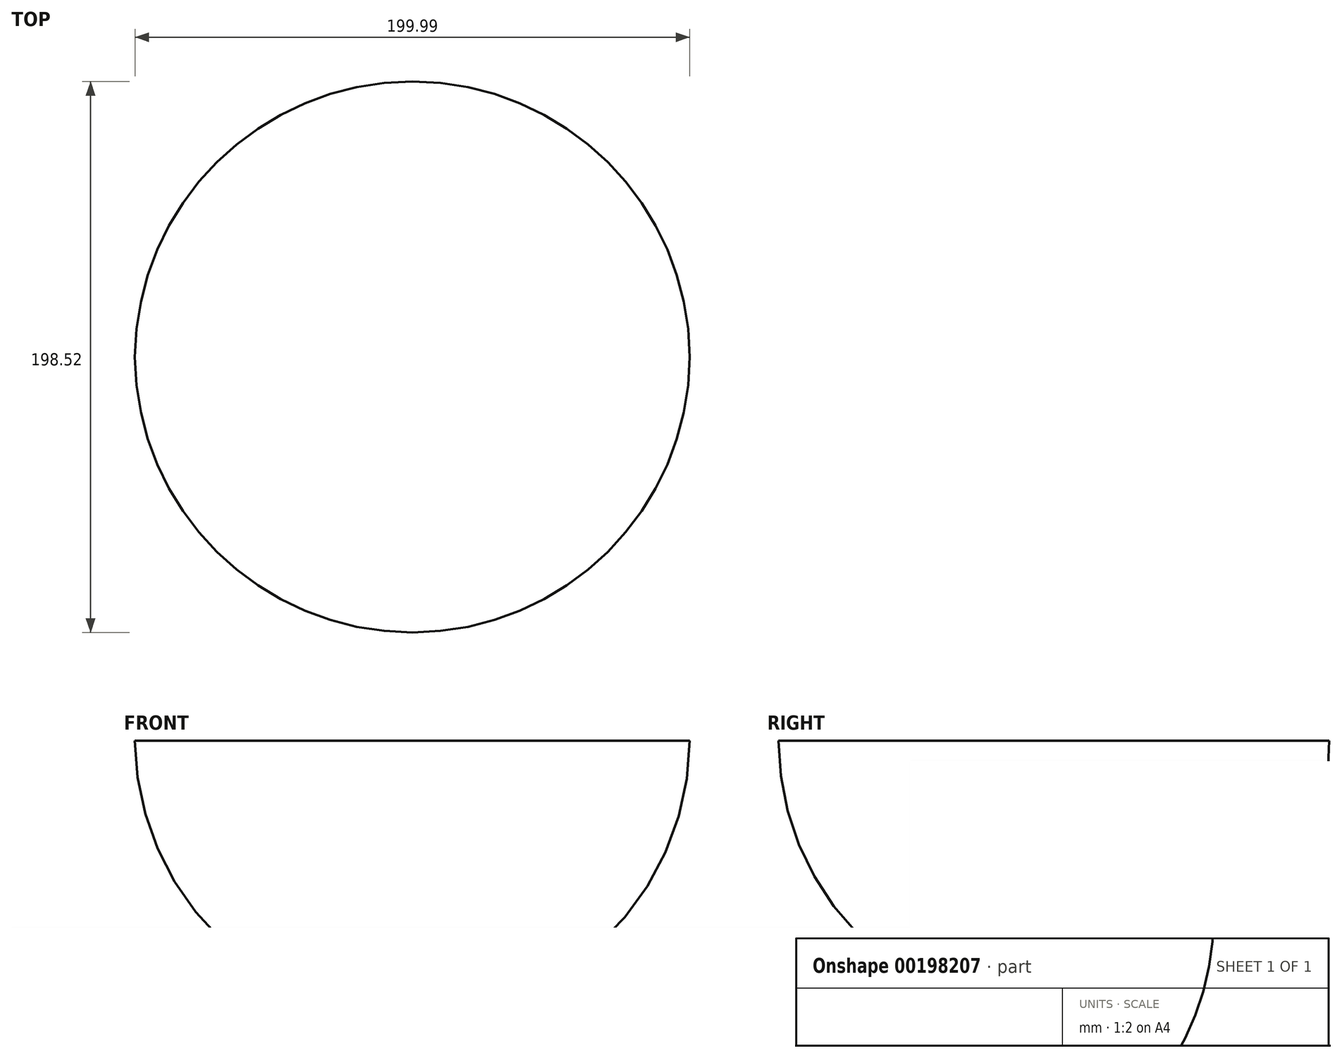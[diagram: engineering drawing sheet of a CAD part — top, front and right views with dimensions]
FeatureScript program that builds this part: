
annotation { "Feature Type Name" : "Feature", "Feature Type Description" : "" }
export const myFeature = defineFeature(function(context is Context, id is Id, definition is map)
    precondition{}
    {
        {
            var Q0;
            Q0=qCreatedBy(makeId("Top.planeOp"),FACE);
            var sketch = newSketch(context, id + "F0", { "sketchPlane" : qUnion([Q0])});
            skLineSegment(sketch, "E0", {"start": v(-124.05, 0) * mm, "end": v(134.98, 0) * mm});
            skArc(sketch, "E1", {"start": v(-100.93, 0) * mm, "mid": v(-0.94, -99.26) * mm, "end": v(99.06, 0) * mm});
            skSolve(sketch);
        }
        {
            var Q0;
            Q0 = qSketchRegion(id + "F0", true);
            var Q1;
            Q1=sQuery(id+"F0.wireOp",EDGE,"E0");
            revolve(context, id + "F1", {"entities" : qUnion([Q0]), "axis" : qUnion([Q1]), "revolveType" : RevolveType.ONE_DIRECTION, "angle" : 180 * degree});
        }
    });
